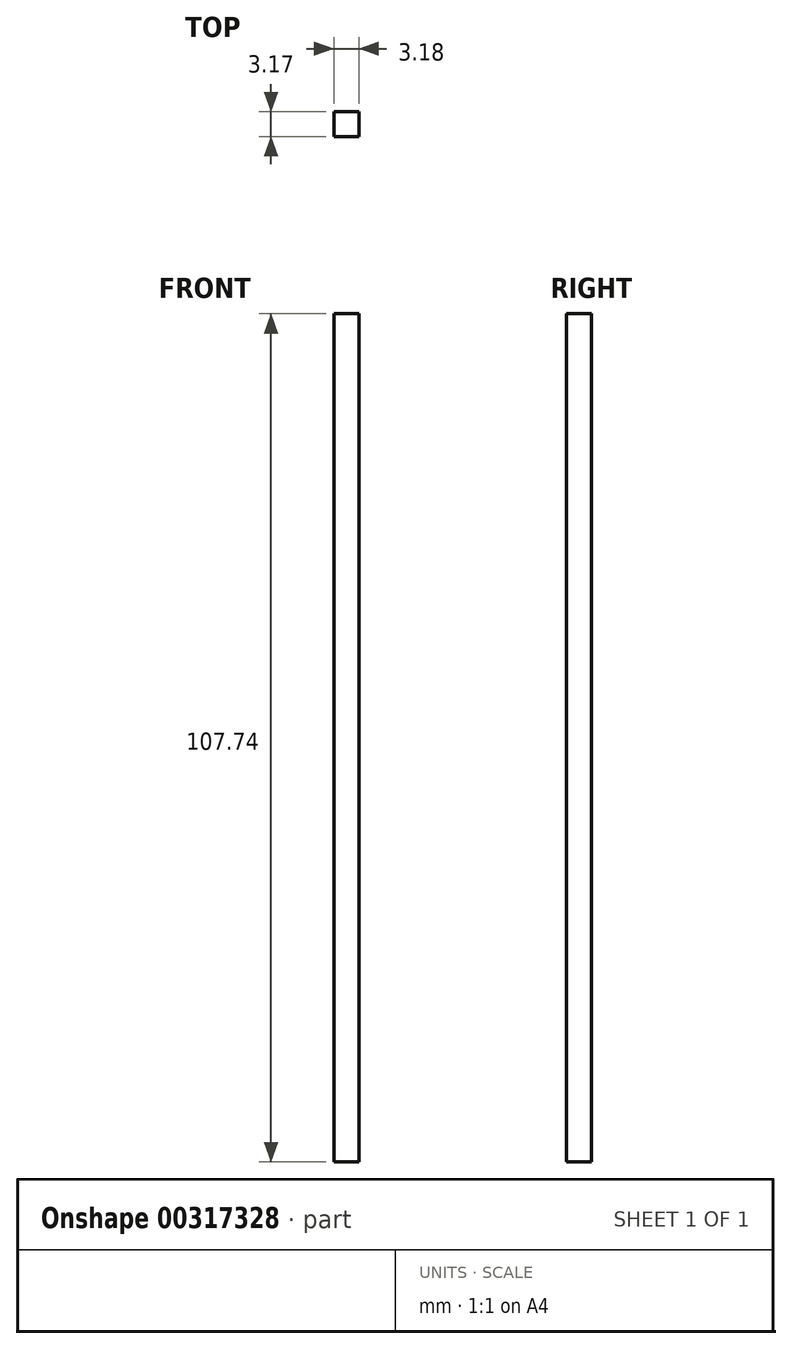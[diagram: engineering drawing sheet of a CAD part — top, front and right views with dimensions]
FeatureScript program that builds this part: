
annotation { "Feature Type Name" : "Feature", "Feature Type Description" : "" }
export const myFeature = defineFeature(function(context is Context, id is Id, definition is map)
    precondition{}
    {
        {
            var Q0;
            Q0=qCreatedBy(makeId("Front.planeOp"),FACE);
            var sketch = newSketch(context, id + "F0", { "sketchPlane" : qUnion([Q0])});
            skLineSegment(sketch, "E0.bottom", {"start": v(1.59, 53.87) * mm, "end": v(-1.59, 53.87) * mm});
            skLineSegment(sketch, "E0.top", {"start": v(1.59, -53.87) * mm, "end": v(-1.59, -53.87) * mm});
            skLineSegment(sketch, "E0.left", {"start": v(1.59, 53.87) * mm, "end": v(1.59, -53.87) * mm});
            skLineSegment(sketch, "E0.right", {"start": v(-1.59, 53.87) * mm, "end": v(-1.59, -53.87) * mm});
            skPoint(sketch, "E0.middle", {"position": v(0, 0) * mm});
            skSolve(sketch);
        }
        {
            var Q0;
            Q0 = qSketchRegion(id + "F0", true);
            extrude(context, id + "F1", {"entities" : qUnion([Q0]), "depth" : 3.17 * mm});
        }
    });
